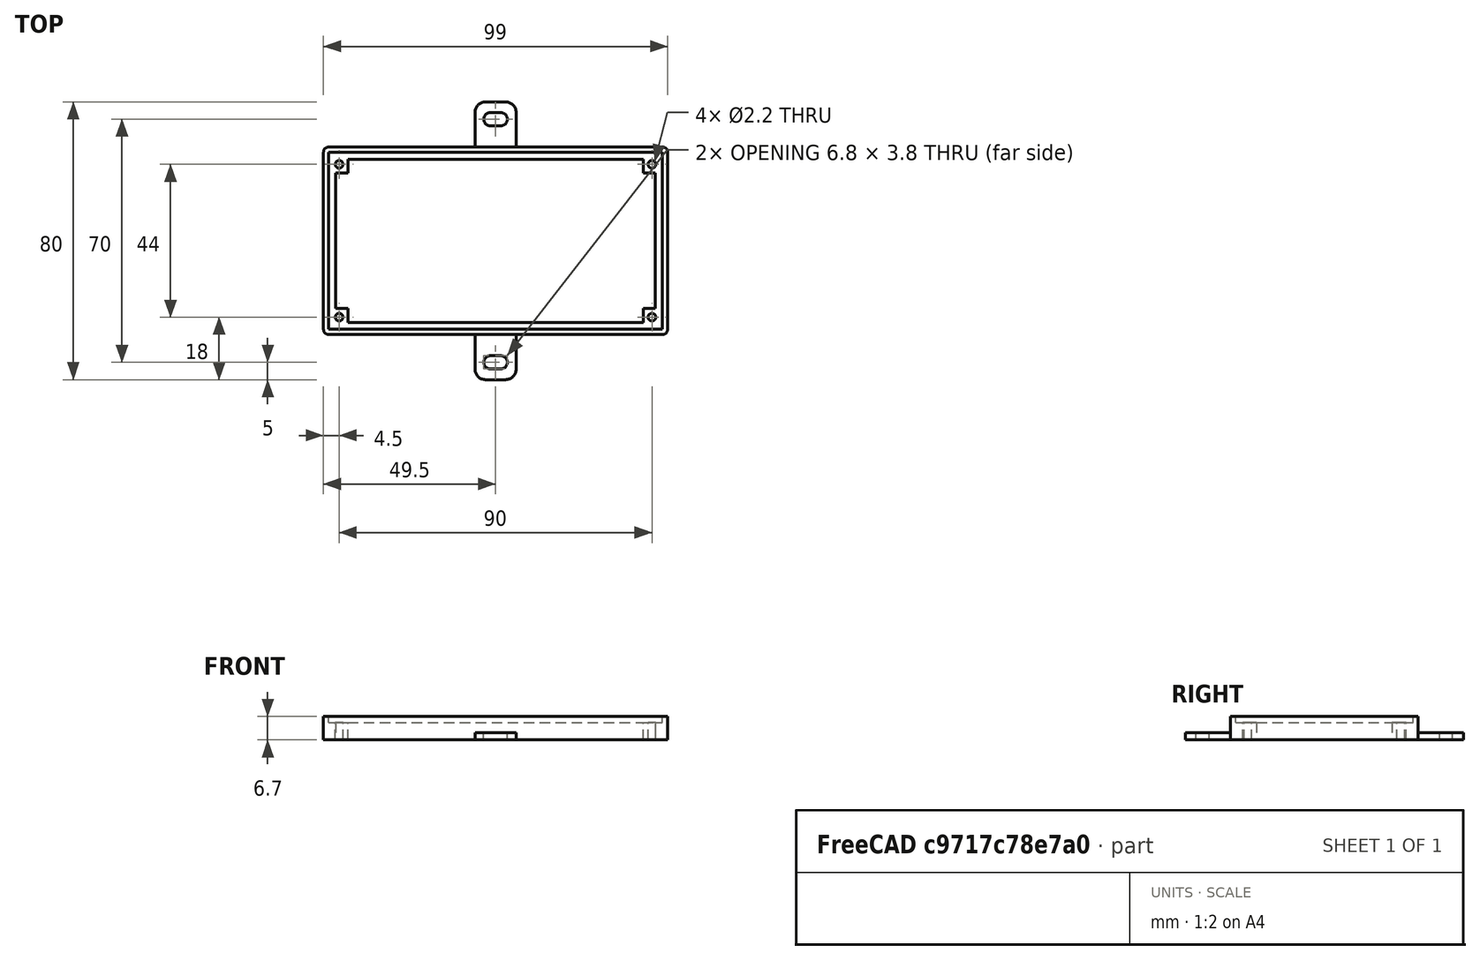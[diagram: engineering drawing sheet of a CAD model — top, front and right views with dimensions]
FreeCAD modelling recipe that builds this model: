
FCSTD DOCUMENT  (FreeCAD 0.19R23578 (Git))
Label: nrf51822_programmer
License: All rights reserved
LicenseURL: http://en.wikipedia.org/wiki/All_rights_reserved
objects: Part::Box×4, Part::MultiFuse×3, Part::FeaturePython×2, Part::Cut×2, Spreadsheet::Sheet×1, Part::Cylinder×1, Part::Fillet×1, Part::Feature×1, App::Part×1
note: 14 computed .brp shape members not serialized (recipe doc carries the construction recipe); baked Part::Feature solids carry a one-line shape summary decoded from their .brp

FEATURE [Spreadsheet::Sheet] Spreadsheet  label="p"
  cells = A1=hole_x_dist; B1(hole_x_dist)=90; A2=hole_y_dist; B2(hole_y_dist)=44; A3=pcb_under; B3(pcb_under)=2; A4=pcb_x; B4(pcb_x)=96; A5=pcb_y; B5(pcb_y)=51; A6=hole_stand_x; B6(hole_stand_x)=5.5; A7=hole_stand_y; B7(hole_stand_y)=6; A8=hole_r; B8(hole_r)=1.1; A9=box_wall; B9(box_wall)=1.5; A10=under_layer; B10(under_layer)=3; A11=pcb_height; B11(pcb_height)=1.7; A12=under_pcb_border; B12(under_pcb_border)=2
FEATURE [Part::Box] Box  label="bottom cube"
  AttacherType = Attacher::AttachEngine3D
  Height = 6.7
  Length = 99
  Width = 54
  expr: Height = <<p>>.pcb_under + <<p>>.pcb_height + <<p>>.under_layer
  expr: Length = <<p>>.pcb_x + <<p>>.box_wall * 2
  expr: Width = <<p>>.pcb_y + <<p>>.box_wall * 2
FEATURE [Part::Box] Box001  label="bottom extraction"
  AttacherType = Attacher::AttachEngine3D
  Height = 10
  Length = 92
  Placement = pos=(3.5,3.5,0) rot=(0,0,1;0rad)
  Width = 47
  expr: Width = <<p>>.pcb_y - <<p>>.under_pcb_border * 2
  expr: Length = <<p>>.pcb_x - <<p>>.under_pcb_border * 2
  expr: .Placement.Base.x = <<p>>.under_pcb_border + <<p>>.box_wall
  expr: .Placement.Base.y = <<p>>.under_pcb_border + <<p>>.box_wall
FEATURE [Part::Box] Box002  label="pcb extraction"
  AttacherType = Attacher::AttachEngine3D
  Height = 10
  Length = 96
  Placement = pos=(1.5,1.5,5) rot=(0,0,1;0rad)
  Width = 51
  expr: Width = <<p>>.pcb_y
  expr: Length = <<p>>.pcb_x
  expr: .Placement.Base.x = <<p>>.box_wall
  expr: .Placement.Base.y = <<p>>.box_wall
  expr: .Placement.Base.z = <<p>>.under_pcb_border + <<p>>.under_layer
FEATURE [Part::MultiFuse] Fusion  label="bottom extraction001"
  Shapes = -> [Box001,Box002]
FEATURE [Part::Box] Box003  label="hole stand cube"
  AttacherType = Attacher::AttachEngine3D
  Height = 5
  Length = 5.5
  Placement = pos=(1.5,1.5,0) rot=(0,0,1;0rad)
  Width = 6
  expr: Length = <<p>>.hole_stand_x
  expr: Width = <<p>>.hole_stand_y
  expr: Height = <<p>>.pcb_under + <<p>>.under_layer
  expr: .Placement.Base.x = <<p>>.box_wall
  expr: .Placement.Base.y = <<p>>.box_wall
FEATURE [Part::FeaturePython] Array  label="hole stand array"  # Draft array (typed FeaturePython)
  Angle = 360
  ArrayType = 0
  Axis = (0,0,1)
  Base = -> Box003
  Center = (0,0,0)
  Fuse = false
  IntervalAxis = (0,0,0)
  IntervalX = (90.5,0,0)
  IntervalY = (0,45,0)
  IntervalZ = (0,0,1)
  NumberPolar = 1
  NumberX = 2
  NumberY = 2
  NumberZ = 1
  expr: .IntervalX.x = <<p>>.pcb_x - <<p>>.hole_stand_x
  expr: .IntervalY.y = <<p>>.pcb_y - <<p>>.hole_stand_y
FEATURE [Part::Cylinder] Cylinder  label="pcb hole"
  Angle = 360
  AttacherType = Attacher::AttachEngine3D
  Height = 10
  Placement = pos=(4.5,5,0) rot=(0,0,1;0rad)
  Radius = 1.1
  expr: Radius = <<p>>.hole_r
  expr: .Placement.Base.x = (<<p>>.box_wall * 2 + <<p>>.pcb_x - <<p>>.hole_x_dist) / 2
  expr: .Placement.Base.y = (<<p>>.box_wall * 2 + <<p>>.pcb_y - <<p>>.hole_y_dist) / 2
FEATURE [Part::FeaturePython] Array001  label="hole array"  # Draft array (typed FeaturePython)
  Angle = 360
  ArrayType = 0
  Axis = (0,0,1)
  Base = -> Cylinder
  Center = (0,0,0)
  Fuse = false
  IntervalAxis = (0,0,0)
  IntervalX = (90,0,0)
  IntervalY = (0,44,0)
  IntervalZ = (0,0,1)
  NumberPolar = 1
  NumberX = 2
  NumberY = 2
  NumberZ = 1
  expr: .IntervalX.x = <<p>>.hole_x_dist
  expr: .IntervalY.y = <<p>>.hole_y_dist
FEATURE [Part::Fillet] Fillet001  label="bottom cube fillet"
  Base = -> Box
  Edges = 4 edges r=1.5: [Edge1,Edge3,Edge5,Edge7]
FEATURE [Part::Feature] Cut002002  label="attach plane y dir002"
  Placement = pos=(43.6,-13,0) rot=(0,0,1;0rad)
  shape: bbox 11.8 x 80 x 2 mm, 20 faces (baked)
FEATURE [Part::MultiFuse] Fusion002  label="bottom fusion"
  Shapes = -> [Fillet001,Cut002002]
FEATURE [Part::Cut] Cut  label="pcb box cut"
  Base = -> Fusion002
  Tool = -> Fusion
FEATURE [Part::MultiFuse] Fusion001  label="frame fusion"
  Shapes = -> [Array,Cut]
FEATURE [Part::Cut] Cut001  label="frame fusion with holes"
  Base = -> Fusion001
  Tool = -> Array001
FEATURE [App::Part] Part  label="pcb with 4 holes part"
  Group = -> [Fusion,Fusion002,Box002,Box003,Box001,Array001,Box,Cut,Array,Cylinder,Fusion001,Cut001]
  Origin = -> Origin
